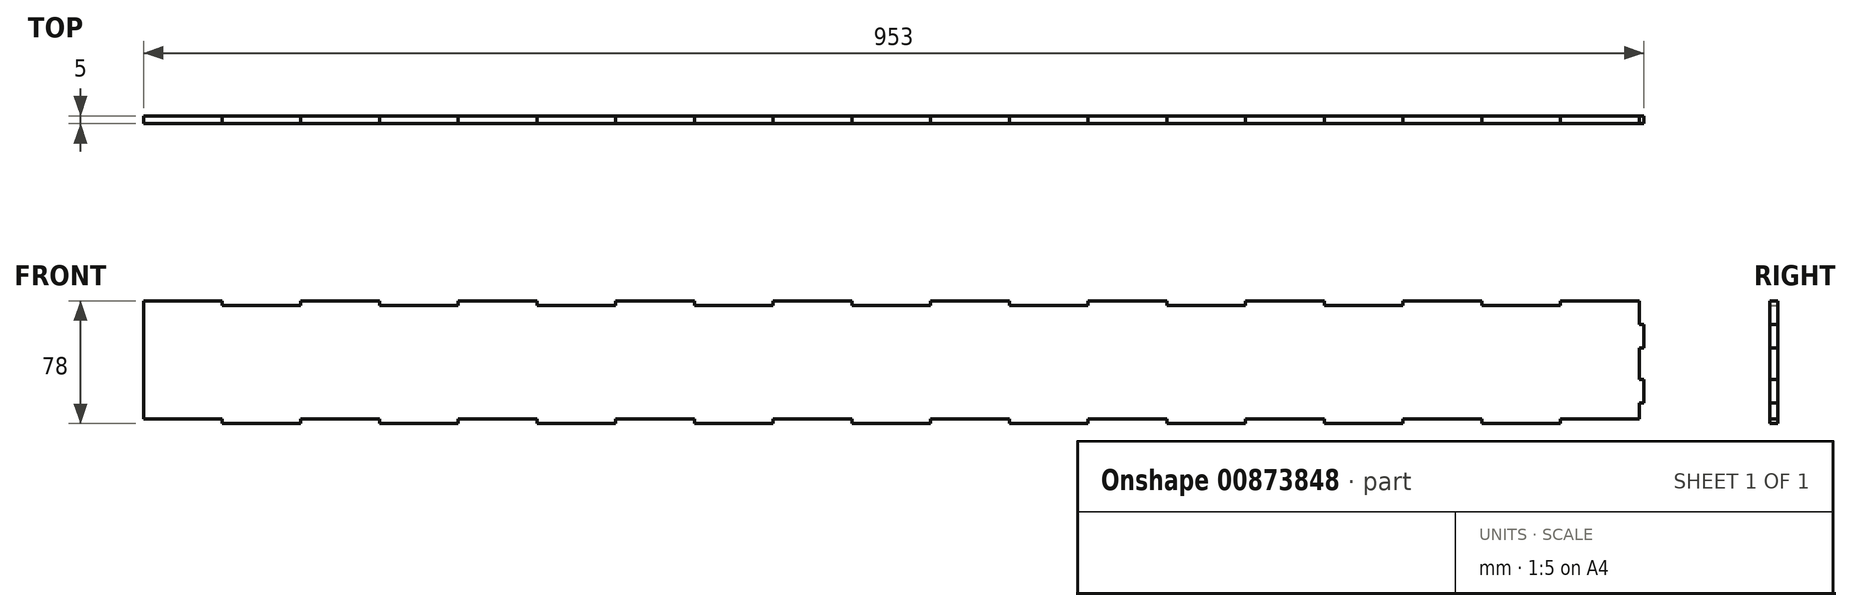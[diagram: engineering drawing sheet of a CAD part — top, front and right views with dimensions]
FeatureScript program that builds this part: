
annotation { "Feature Type Name" : "Feature", "Feature Type Description" : "" }
export const myFeature = defineFeature(function(context is Context, id is Id, definition is map)
    precondition{}
    {
        {
            var Q0;
            Q0=qCreatedBy(makeId("Front.planeOp"),FACE);
            var sketch = newSketch(context, id + "F0", { "sketchPlane" : qUnion([Q0])});
            skLineSegment(sketch, "E0.bottom", {"start": v(-425, 35) * mm, "end": v(-375, 35) * mm});
            skLineSegment(sketch, "E0.top", {"start": v(-475, -37) * mm, "end": v(-425, -37) * mm});
            skLineSegment(sketch, "E0.left", {"start": v(-475, 35) * mm, "end": v(-475, -37) * mm});
            skLineSegment(sketch, "E0.right", {"start": v(475, 35) * mm, "end": v(475, 23) * mm});
            skLineSegment(sketch, "E1", {"start": v(-425, -37) * mm, "end": v(-425, -40) * mm});
            skLineSegment(sketch, "E2", {"start": v(-425, -40) * mm, "end": v(-375, -40) * mm});
            skLineSegment(sketch, "E3", {"start": v(-375, -40) * mm, "end": v(-375, -37) * mm});
            skLineSegment(sketch, "E4", {"start": v(-475, 35) * mm, "end": v(-475, 38) * mm});
            skLineSegment(sketch, "E5", {"start": v(-475, 38) * mm, "end": v(-425, 38) * mm});
            skLineSegment(sketch, "E6", {"start": v(-425, 38) * mm, "end": v(-425, 35) * mm});
            skLineSegment(sketch, "E7.1.0.0", {"start": v(-325, -40) * mm, "end": v(-275, -40) * mm});
            skLineSegment(sketch, "E7.1.0.1", {"start": v(-275, -40) * mm, "end": v(-275, -37) * mm});
            skLineSegment(sketch, "E7.1.0.2", {"start": v(-325, -37) * mm, "end": v(-325, -40) * mm});
            skLineSegment(sketch, "E7.1.0.3", {"start": v(-375, 38) * mm, "end": v(-325, 38) * mm});
            skLineSegment(sketch, "E7.1.0.4", {"start": v(-325, 38) * mm, "end": v(-325, 35) * mm});
            skLineSegment(sketch, "E7.1.0.5", {"start": v(-375, 35) * mm, "end": v(-375, 38) * mm});
            skLineSegment(sketch, "E7.2.0.0", {"start": v(-225, -40) * mm, "end": v(-175, -40) * mm});
            skLineSegment(sketch, "E7.2.0.1", {"start": v(-175, -40) * mm, "end": v(-175, -37) * mm});
            skLineSegment(sketch, "E7.2.0.2", {"start": v(-225, -37) * mm, "end": v(-225, -40) * mm});
            skLineSegment(sketch, "E7.2.0.3", {"start": v(-275, 38) * mm, "end": v(-225, 38) * mm});
            skLineSegment(sketch, "E7.2.0.4", {"start": v(-225, 38) * mm, "end": v(-225, 35) * mm});
            skLineSegment(sketch, "E7.2.0.5", {"start": v(-275, 35) * mm, "end": v(-275, 38) * mm});
            skLineSegment(sketch, "E7.3.0.0", {"start": v(-125, -40) * mm, "end": v(-75, -40) * mm});
            skLineSegment(sketch, "E7.3.0.1", {"start": v(-75, -40) * mm, "end": v(-75, -37) * mm});
            skLineSegment(sketch, "E7.3.0.2", {"start": v(-125, -37) * mm, "end": v(-125, -40) * mm});
            skLineSegment(sketch, "E7.3.0.3", {"start": v(-175, 38) * mm, "end": v(-125, 38) * mm});
            skLineSegment(sketch, "E7.3.0.4", {"start": v(-125, 38) * mm, "end": v(-125, 35) * mm});
            skLineSegment(sketch, "E7.3.0.5", {"start": v(-175, 35) * mm, "end": v(-175, 38) * mm});
            skLineSegment(sketch, "E7.4.0.0", {"start": v(-25, -40) * mm, "end": v(25, -40) * mm});
            skLineSegment(sketch, "E7.4.0.1", {"start": v(25, -40) * mm, "end": v(25, -37) * mm});
            skLineSegment(sketch, "E7.4.0.2", {"start": v(-25, -37) * mm, "end": v(-25, -40) * mm});
            skLineSegment(sketch, "E7.4.0.3", {"start": v(-75, 38) * mm, "end": v(-25, 38) * mm});
            skLineSegment(sketch, "E7.4.0.4", {"start": v(-25, 38) * mm, "end": v(-25, 35) * mm});
            skLineSegment(sketch, "E7.4.0.5", {"start": v(-75, 35) * mm, "end": v(-75, 38) * mm});
            skLineSegment(sketch, "E7.5.0.0", {"start": v(75, -40) * mm, "end": v(125, -40) * mm});
            skLineSegment(sketch, "E7.5.0.1", {"start": v(125, -40) * mm, "end": v(125, -37) * mm});
            skLineSegment(sketch, "E7.5.0.2", {"start": v(75, -37) * mm, "end": v(75, -40) * mm});
            skLineSegment(sketch, "E7.5.0.3", {"start": v(25, 38) * mm, "end": v(75, 38) * mm});
            skLineSegment(sketch, "E7.5.0.4", {"start": v(75, 38) * mm, "end": v(75, 35) * mm});
            skLineSegment(sketch, "E7.5.0.5", {"start": v(25, 35) * mm, "end": v(25, 38) * mm});
            skLineSegment(sketch, "E7.6.0.0", {"start": v(175, -40) * mm, "end": v(225, -40) * mm});
            skLineSegment(sketch, "E7.6.0.1", {"start": v(225, -40) * mm, "end": v(225, -37) * mm});
            skLineSegment(sketch, "E7.6.0.2", {"start": v(175, -37) * mm, "end": v(175, -40) * mm});
            skLineSegment(sketch, "E7.6.0.3", {"start": v(125, 38) * mm, "end": v(175, 38) * mm});
            skLineSegment(sketch, "E7.6.0.4", {"start": v(175, 38) * mm, "end": v(175, 35) * mm});
            skLineSegment(sketch, "E7.6.0.5", {"start": v(125, 35) * mm, "end": v(125, 38) * mm});
            skLineSegment(sketch, "E7.7.0.0", {"start": v(275, -40) * mm, "end": v(325, -40) * mm});
            skLineSegment(sketch, "E7.7.0.1", {"start": v(325, -40) * mm, "end": v(325, -37) * mm});
            skLineSegment(sketch, "E7.7.0.2", {"start": v(275, -37) * mm, "end": v(275, -40) * mm});
            skLineSegment(sketch, "E7.7.0.3", {"start": v(225, 38) * mm, "end": v(275, 38) * mm});
            skLineSegment(sketch, "E7.7.0.4", {"start": v(275, 38) * mm, "end": v(275, 35) * mm});
            skLineSegment(sketch, "E7.7.0.5", {"start": v(225, 35) * mm, "end": v(225, 38) * mm});
            skLineSegment(sketch, "E7.8.0.0", {"start": v(375, -40) * mm, "end": v(425, -40) * mm});
            skLineSegment(sketch, "E7.8.0.1", {"start": v(425, -40) * mm, "end": v(425, -37) * mm});
            skLineSegment(sketch, "E7.8.0.2", {"start": v(375, -37) * mm, "end": v(375, -40) * mm});
            skLineSegment(sketch, "E7.8.0.3", {"start": v(325, 38) * mm, "end": v(375, 38) * mm});
            skLineSegment(sketch, "E7.8.0.4", {"start": v(375, 38) * mm, "end": v(375, 35) * mm});
            skLineSegment(sketch, "E7.8.0.5", {"start": v(325, 35) * mm, "end": v(325, 38) * mm});
            skLineSegment(sketch, "E7.direction1", {"start": v(-425, -40) * mm, "end": v(-325, -40) * mm, "construction": true});
            skLineSegment(sketch, "E8.1.0.0", {"start": v(425, 38) * mm, "end": v(475, 38) * mm});
            skLineSegment(sketch, "E8.1.0.1", {"start": v(475, 38) * mm, "end": v(475, 35) * mm});
            skLineSegment(sketch, "E8.1.0.2", {"start": v(425, 35) * mm, "end": v(425, 38) * mm});
            skLineSegment(sketch, "E8.direction1", {"start": v(375, 35) * mm, "end": v(425, 35) * mm, "construction": true});
            skLineSegment(sketch, "E9", {"start": v(475, 23) * mm, "end": v(478, 23) * mm});
            skLineSegment(sketch, "E10", {"start": v(478, 23) * mm, "end": v(478, 8) * mm});
            skLineSegment(sketch, "E11", {"start": v(478, 8) * mm, "end": v(475, 8) * mm});
            skLineSegment(sketch, "E12", {"start": v(475, -12) * mm, "end": v(478, -12) * mm});
            skLineSegment(sketch, "E13", {"start": v(478, -12) * mm, "end": v(478, -27) * mm});
            skLineSegment(sketch, "E14", {"start": v(478, -27) * mm, "end": v(475, -27) * mm});
            skLineSegment(sketch, "E15.trimOffspring", {"start": v(-325, 35) * mm, "end": v(-275, 35) * mm});
            skLineSegment(sketch, "E16.trimOffspring", {"start": v(-225, 35) * mm, "end": v(-175, 35) * mm});
            skLineSegment(sketch, "E17.trimOffspring", {"start": v(-125, 35) * mm, "end": v(-75, 35) * mm});
            skLineSegment(sketch, "E18.trimOffspring", {"start": v(-25, 35) * mm, "end": v(25, 35) * mm});
            skLineSegment(sketch, "E19.trimOffspring", {"start": v(75, 35) * mm, "end": v(125, 35) * mm});
            skLineSegment(sketch, "E20.trimOffspring", {"start": v(175, 35) * mm, "end": v(225, 35) * mm});
            skLineSegment(sketch, "E21.trimOffspring", {"start": v(275, 35) * mm, "end": v(325, 35) * mm});
            skLineSegment(sketch, "E22.trimOffspring", {"start": v(375, 35) * mm, "end": v(425, 35) * mm});
            skLineSegment(sketch, "E23.trimOffspring", {"start": v(425, -37) * mm, "end": v(475, -37) * mm});
            skLineSegment(sketch, "E24.trimOffspring", {"start": v(325, -37) * mm, "end": v(375, -37) * mm});
            skLineSegment(sketch, "E25.trimOffspring", {"start": v(225, -37) * mm, "end": v(275, -37) * mm});
            skLineSegment(sketch, "E26.trimOffspring", {"start": v(125, -37) * mm, "end": v(175, -37) * mm});
            skLineSegment(sketch, "E27.trimOffspring", {"start": v(25, -37) * mm, "end": v(75, -37) * mm});
            skLineSegment(sketch, "E28.trimOffspring", {"start": v(-75, -37) * mm, "end": v(-25, -37) * mm});
            skLineSegment(sketch, "E29.trimOffspring", {"start": v(-175, -37) * mm, "end": v(-125, -37) * mm});
            skLineSegment(sketch, "E30.trimOffspring", {"start": v(-275, -37) * mm, "end": v(-225, -37) * mm});
            skLineSegment(sketch, "E31.trimOffspring", {"start": v(-375, -37) * mm, "end": v(-325, -37) * mm});
            skLineSegment(sketch, "E32.trimOffspring", {"start": v(475, 8) * mm, "end": v(475, -12) * mm});
            skLineSegment(sketch, "E33.trimOffspring", {"start": v(475, -27) * mm, "end": v(475, -37) * mm});
            skSolve(sketch);
        }
        {
            var Q0;
            Q0 = qSketchRegion(id + "F0", true);
            extrude(context, id + "F1", {"entities" : qUnion([Q0]), "depth" : 5 * mm, "offsetDistance" : 25 * mm});
        }
    });
